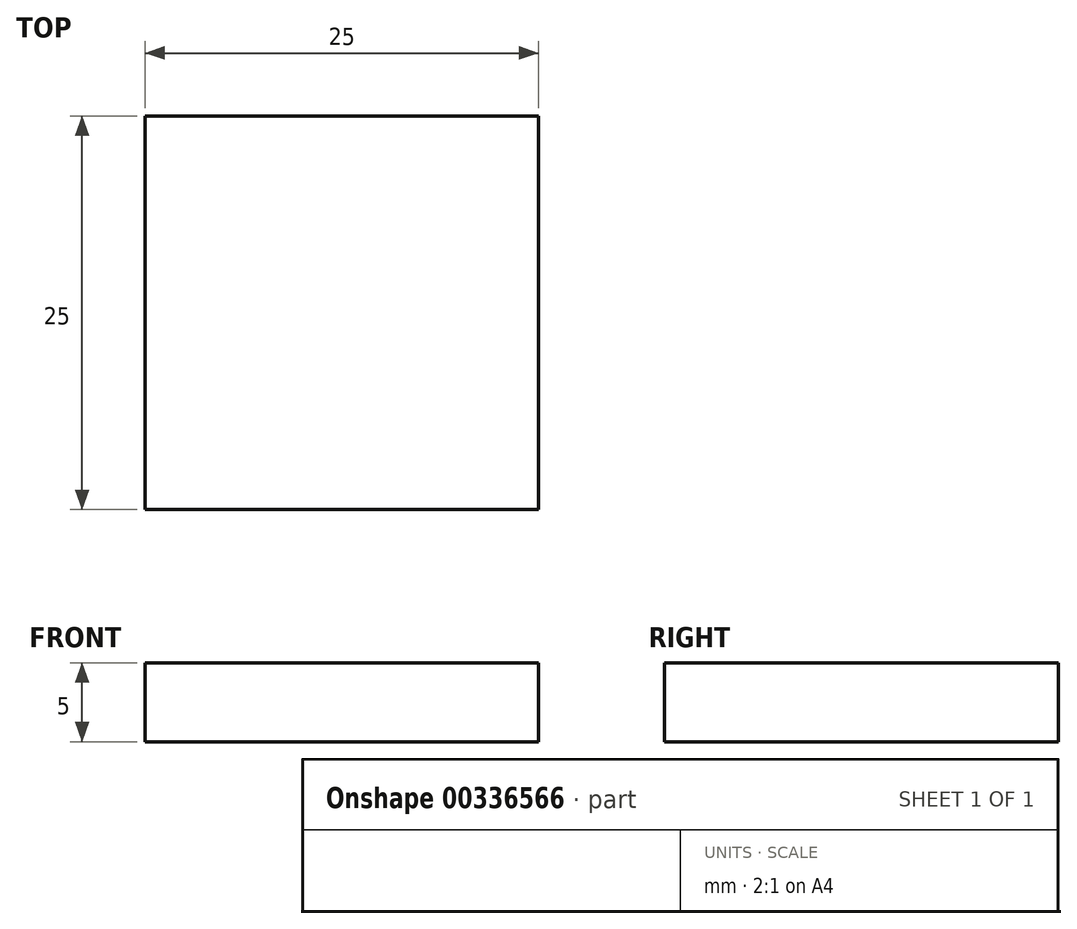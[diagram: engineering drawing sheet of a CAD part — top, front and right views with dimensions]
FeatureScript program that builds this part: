
annotation { "Feature Type Name" : "Feature", "Feature Type Description" : "" }
export const myFeature = defineFeature(function(context is Context, id is Id, definition is map)
    precondition{}
    {
        {
            var Q0;
            Q0=qCreatedBy(makeId("Front.planeOp"),FACE);
            var sketch = newSketch(context, id + "F0", { "sketchPlane" : qUnion([Q0])});
            skLineSegment(sketch, "E0.bottom", {"start": v(0, 0) * mm, "end": v(25, 0) * mm});
            skLineSegment(sketch, "E0.top", {"start": v(0, 5) * mm, "end": v(25, 5) * mm});
            skLineSegment(sketch, "E0.left", {"start": v(0, 0) * mm, "end": v(0, 5) * mm});
            skLineSegment(sketch, "E0.right", {"start": v(25, 0) * mm, "end": v(25, 5) * mm});
            skSolve(sketch);
        }
        {
            var Q0;
            Q0 = qSketchRegion(id + "F0", true);
            extrude(context, id + "F1", {"entities" : qUnion([Q0]), "depth" : 25 * mm});
        }
    });
